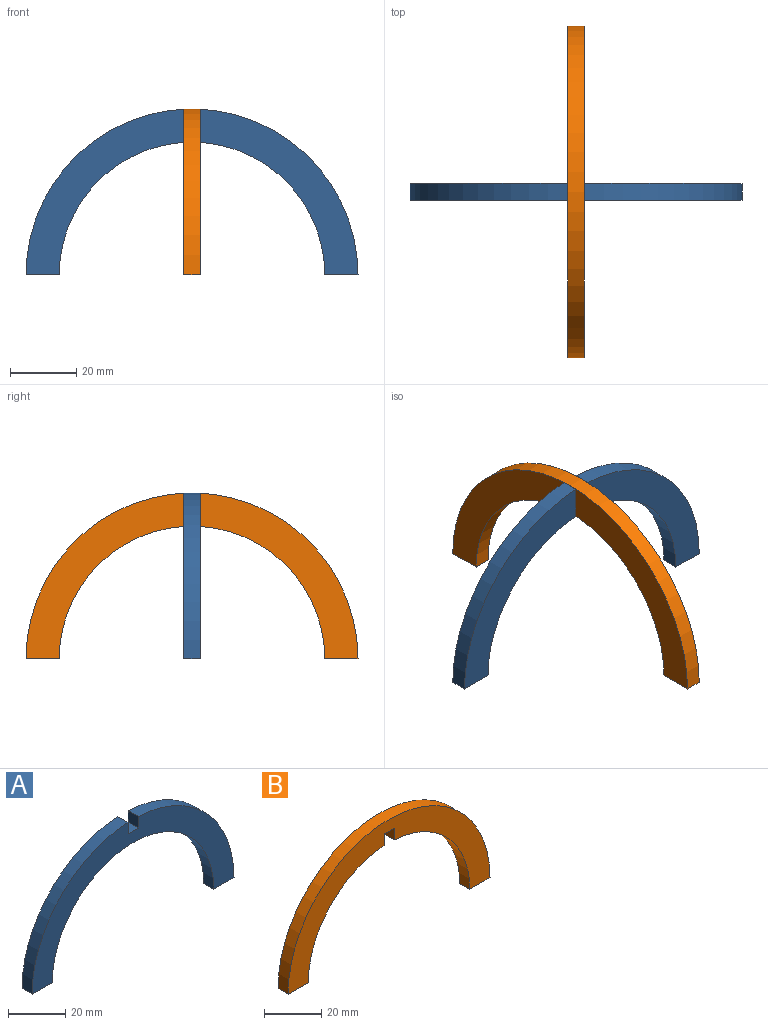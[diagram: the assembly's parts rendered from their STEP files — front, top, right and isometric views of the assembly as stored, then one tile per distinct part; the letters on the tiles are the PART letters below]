
ASSEMBLY  parts=2 mates=1
PART A: 10 faces, bbox 100x5x49.9 mm
  f0: cylinder r=40mm len=80mm, axis (0,-1,0), area 628.3mm2, adj f1,f7,f8,f9
  f1: plane 10x5mm, normal (0,0,-1), area 50mm2, adj f0,f2,f8,f9
  f2: cylinder r=50mm len=49.94mm, axis (0,-1,0), area 380.2mm2, adj f1,f3,f8,f9
  f3: plane 5x4.94mm, normal (-1,0,0), area 24.7mm2, adj f2,f4,f8,f9
  f4: plane 5x5mm, normal (0,0,1), area 25mm2, adj f3,f5,f8,f9
  f5: plane 5x4.94mm, normal (1,0,0), area 24.7mm2, adj f4,f6,f8,f9
  f6: cylinder r=50mm len=49.94mm, axis (0,-1,0), area 380.2mm2, adj f5,f7,f8,f9
  f7: plane 10x5mm, normal (0,0,-1), area 50mm2, adj f0,f6,f8,f9
  f8: plane 100x49.94mm, normal (0,1,0), area 1388.8mm2, adj f0,f1,f2,f3,f4,f5,f6,f7
  f9: plane 100x49.94mm, normal (0,-1,0), area 1388.8mm2, adj f0,f1,f2,f3,f4,f5,f6,f7
PART B: 10 faces, bbox 100x5x50 mm
  f0: plane 5x5mm, normal (0,0,-1), area 25mm2, adj f1,f7,f8,f9
  f1: plane 5.08x5mm, normal (-1,0,0), area 25.4mm2, adj f0,f2,f8,f9
  f2: cylinder r=40mm len=39.92mm, axis (0,1,0), area 301.7mm2, adj f1,f3,f8,f9
  f3: plane 10x5mm, normal (0,0,-1), area 50mm2, adj f2,f4,f8,f9
  f4: cylinder r=50mm len=100mm, axis (0,1,0), area 785.4mm2, adj f3,f5,f8,f9
  f5: plane 10x5mm, normal (0,0,-1), area 50mm2, adj f4,f6,f8,f9
  f6: cylinder r=40mm len=39.92mm, axis (0,1,0), area 301.7mm2, adj f5,f7,f8,f9
  f7: plane 5.08x5mm, normal (1,0,0), area 25.4mm2, adj f0,f6,f8,f9
  f8: plane 100x50mm, normal (0,-1,0), area 1388.6mm2, adj f0,f1,f2,f3,f4,f5,f6,f7
  f9: plane 100x50mm, normal (0,1,0), area 1388.6mm2, adj f0,f1,f2,f3,f4,f5,f6,f7
PLACE A t=(-26.39,-7.24,-9.23)mm
PLACE B rot(axis=(0,0,1),90deg) t=(-28.89,-4.74,-9.23)mm
MATE fastened B.f0 <-> A.f4  axis (0,0,-1) through (-26.39,-4.74,35.77)mm
